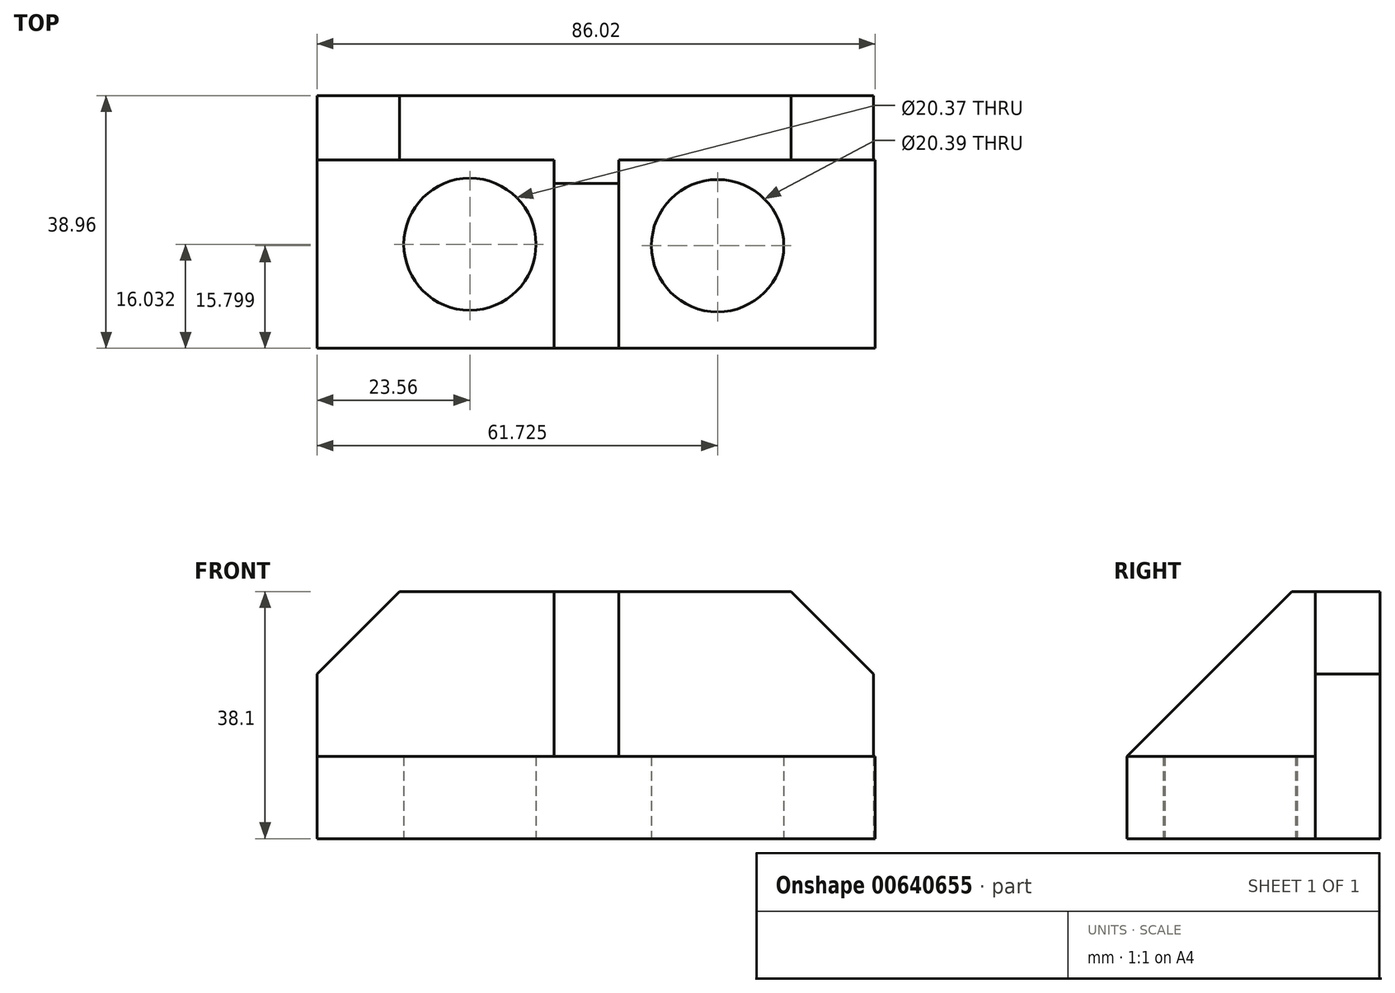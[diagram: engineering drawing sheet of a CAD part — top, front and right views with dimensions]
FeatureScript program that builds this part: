
annotation { "Feature Type Name" : "Feature", "Feature Type Description" : "" }
export const myFeature = defineFeature(function(context is Context, id is Id, definition is map)
    precondition{}
    {
        {
            var Q0;
            Q0=qCreatedBy(makeId("Top.planeOp"),FACE);
            var sketch = newSketch(context, id + "F0", { "sketchPlane" : qUnion([Q0])});
            skLineSegment(sketch, "E0.bottom", {"start": v(34.93, 0) * mm, "end": v(-51.1, 0) * mm});
            skLineSegment(sketch, "E0.top", {"start": v(34.93, 29.03) * mm, "end": v(-51.1, 29.03) * mm});
            skLineSegment(sketch, "E0.left", {"start": v(34.93, 0) * mm, "end": v(34.93, 29.03) * mm});
            skLineSegment(sketch, "E0.right", {"start": v(-51.1, 0) * mm, "end": v(-51.1, 29.03) * mm});
            skLineSegment(sketch, "E1.bottom", {"start": v(-51.1, 29.03) * mm, "end": v(34.64, 29.03) * mm});
            skLineSegment(sketch, "E1.top", {"start": v(-51.1, 38.96) * mm, "end": v(34.64, 38.96) * mm});
            skLineSegment(sketch, "E1.left", {"start": v(-51.1, 29.03) * mm, "end": v(-51.1, 38.96) * mm});
            skLineSegment(sketch, "E1.right", {"start": v(34.64, 29.03) * mm, "end": v(34.64, 38.96) * mm});
            skCircle(sketch, "E2", {"center": v(-27.53, 16.03) * mm, "radius": 10.18 * mm});
            skCircle(sketch, "E3", {"center": v(10.64, 15.8) * mm, "radius": 10.2 * mm});
            skSolve(sketch);
        }
        {
            var Q0;
            Q0 = qSketchRegion(id + "F0", true);
            extrude(context, id + "F1", {"entities" : qUnion([Q0]), "depth" : 12.7 * mm, "offsetDistance" : 25.4 * mm});
        }
        {
            var Q0;
            Q0=makeQuery(id+"F1.opExtrude","CAP_FACE",FACE,{"disambiguationData":[OSD([sQuery(id+"F0.wireOp",EDGE,"E0.bottom"),sQuery(id+"F0.wireOp",EDGE,"E0.left"),sQuery(id+"F0.wireOp",EDGE,"E0.right"),sQuery(id+"F0.wireOp",EDGE,"E1.bottom"),sQuery(id+"F0.wireOp",EDGE,"E1.top"),sQuery(id+"F0.wireOp",EDGE,"E1.left"),sQuery(id+"F0.wireOp",EDGE,"E1.right"),sQuery(id+"F0.wireOp",EDGE,"E2"),sQuery(id+"F0.wireOp",EDGE,"E3")])],"isStart":false});
            var sketch = newSketch(context, id + "F2", { "sketchPlane" : qUnion([Q0])});
            skLineSegment(sketch, "E4.bottom", {"start": v(-51.1, 38.96) * mm, "end": v(34.64, 38.96) * mm});
            skLineSegment(sketch, "E4.top", {"start": v(-51.1, 29.03) * mm, "end": v(34.64, 29.03) * mm});
            skLineSegment(sketch, "E4.left", {"start": v(-51.1, 38.96) * mm, "end": v(-51.1, 29.03) * mm});
            skLineSegment(sketch, "E4.right", {"start": v(34.64, 38.96) * mm, "end": v(34.64, 29.03) * mm});
            skSolve(sketch);
        }
        {
            var Q0;
            Q0=makeQuery(id+"F2.imprint","IMPRINT",FACE,{"disambiguationData":[TD([[makeQuery(id+"F2.imprint","IMPRINT",EDGE,{"derivedFrom":sQuery(id+"F2.wireOp",EDGE,"E4.bottom")}),-1.0]])]});
            extrude(context, id + "F3", {"entities" : qUnion([Q0]), "operationType" : NewBodyOperationType.ADD, "depth" : 25.4 * mm, "offsetDistance" : 25.4 * mm});
        }
        {
            var Q0;
            Q0=makeQuery(id+"F3.opExtrude","CAP_EDGE",EDGE,{"disambiguationData":[OSD([sQuery(id+"F2.wireOp",EDGE,"E4.right")])],"isStart":false});
            chamfer(context, id + "F4", {"entities" : qUnion([Q0]), "width" : 12.7 * mm, "tangentPropagation" : true});
        }
        {
            var Q0;
            Q0=makeQuery(id+"F3.opExtrude","CAP_EDGE",EDGE,{"disambiguationData":[OSD([sQuery(id+"F2.wireOp",EDGE,"E4.left")])],"isStart":false});
            chamfer(context, id + "F5", {"entities" : qUnion([Q0]), "width" : 12.7 * mm, "tangentPropagation" : true});
        }
        {
            var Q0;
            Q0=makeQuery(id+"F1.opExtrude","CAP_FACE",FACE,{"disambiguationData":[OSD([sQuery(id+"F0.wireOp",EDGE,"E0.bottom"),sQuery(id+"F0.wireOp",EDGE,"E0.top"),sQuery(id+"F0.wireOp",EDGE,"E0.left"),sQuery(id+"F0.wireOp",EDGE,"E0.right"),sQuery(id+"F0.wireOp",EDGE,"E1.top"),sQuery(id+"F0.wireOp",EDGE,"E1.left"),sQuery(id+"F0.wireOp",EDGE,"E1.right"),sQuery(id+"F0.wireOp",EDGE,"E2"),sQuery(id+"F0.wireOp",EDGE,"E3")])],"isStart":false});
            var sketch = newSketch(context, id + "F6", { "sketchPlane" : qUnion([Q0])});
            skLineSegment(sketch, "E5.bottom", {"start": v(-14.58, 29.03) * mm, "end": v(-4.62, 29.03) * mm});
            skLineSegment(sketch, "E5.top", {"start": v(-14.58, 0) * mm, "end": v(-4.62, 0) * mm});
            skLineSegment(sketch, "E5.left", {"start": v(-14.58, 29.03) * mm, "end": v(-14.58, 0) * mm});
            skLineSegment(sketch, "E5.right", {"start": v(-4.62, 29.03) * mm, "end": v(-4.62, 0) * mm});
            skSolve(sketch);
        }
        {
            var Q0;
            Q0=makeQuery(id+"F6.imprint","IMPRINT",FACE,{"disambiguationData":[TD([[makeQuery(id+"F6.imprint","IMPRINT",EDGE,{"derivedFrom":sQuery(id+"F6.wireOp",EDGE,"E5.bottom")}),-1.0]])]});
            extrude(context, id + "F7", {"entities" : qUnion([Q0]), "operationType" : NewBodyOperationType.ADD, "depth" : 25.4 * mm, "offsetDistance" : 25.4 * mm});
        }
        {
            var Q0;
            Q0=makeQuery(id+"F7.opExtrude","CAP_EDGE",EDGE,{"disambiguationData":[OSD([sQuery(id+"F6.wireOp",EDGE,"E5.top")])],"isStart":false});
            chamfer(context, id + "F8", {"entities" : qUnion([Q0]), "width" : 25.4 * mm, "tangentPropagation" : true});
        }
    });
